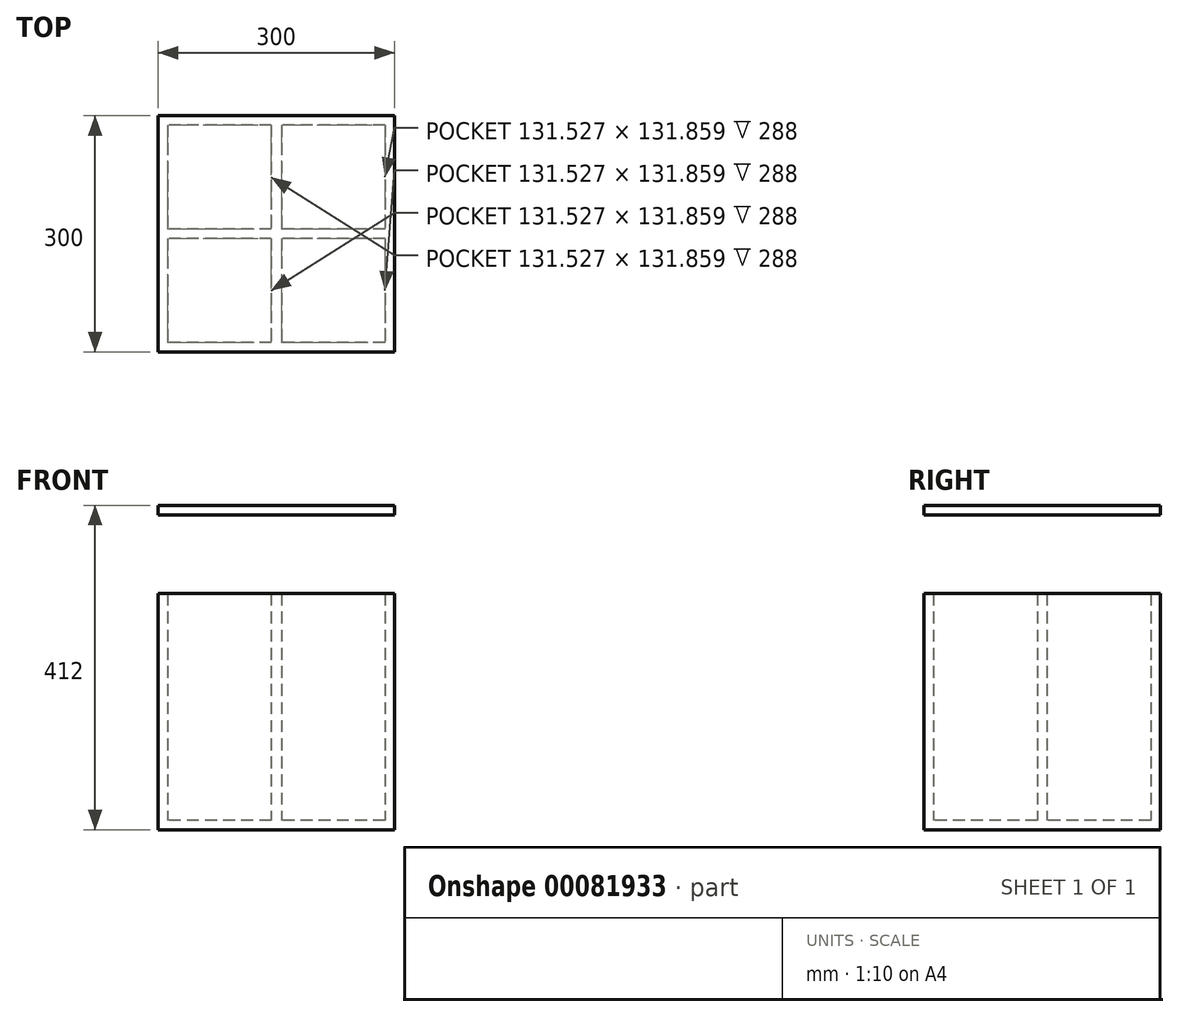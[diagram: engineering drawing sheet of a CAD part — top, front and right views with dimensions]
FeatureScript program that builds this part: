
annotation { "Feature Type Name" : "Feature", "Feature Type Description" : "" }
export const myFeature = defineFeature(function(context is Context, id is Id, definition is map)
    precondition{}
    {
        {
            var Q0;
            Q0=qCreatedBy(makeId("Top.planeOp"),FACE);
            var sketch = newSketch(context, id + "F0", { "sketchPlane" : qUnion([Q0])});
            skLineSegment(sketch, "E0.bottom", {"start": v(150, 150) * mm, "end": v(-150, 150) * mm});
            skLineSegment(sketch, "E0.top", {"start": v(150, -150) * mm, "end": v(-150, -150) * mm});
            skLineSegment(sketch, "E0.left", {"start": v(150, 150) * mm, "end": v(150, -150) * mm});
            skLineSegment(sketch, "E0.right", {"start": v(-150, 150) * mm, "end": v(-150, -150) * mm});
            skPoint(sketch, "E0.middle", {"position": v(0, 0) * mm});
            skSolve(sketch);
        }
        {
            var Q0;
            Q0=makeQuery(id+"F0.imprint","IMPRINT",FACE,{"disambiguationData":[TD([[makeQuery(id+"F0.imprint","IMPRINT",EDGE,{"derivedFrom":sQuery(id+"F0.wireOp",EDGE,"E0.bottom")}),1.0]])]});
            extrude(context, id + "F1", {"entities" : qUnion([Q0]), "depth" : 300 * mm});
        }
        {
            var Q0;
            Q0=makeQuery(id+"F1.opExtrude","CAP_FACE",FACE,{"disambiguationData":[OSD([sQuery(id+"F0.wireOp",EDGE,"E0.bottom"),sQuery(id+"F0.wireOp",EDGE,"E0.top"),sQuery(id+"F0.wireOp",EDGE,"E0.left"),sQuery(id+"F0.wireOp",EDGE,"E0.right")])],"isStart":false});
            shell(context, id + "F2", {"entities" : qUnion([Q0]), "thickness" : 12 * mm});
        }
        {
            var Q0;
            Q0=makeQuery(id+"F2.opShell","OFFSET_FACE",FACE,{"disambiguationData":[OSD([sQuery(id+"F0.wireOp",EDGE,"E0.bottom"),sQuery(id+"F0.wireOp",EDGE,"E0.top"),sQuery(id+"F0.wireOp",EDGE,"E0.left"),sQuery(id+"F0.wireOp",EDGE,"E0.right")])]});
            var sketch = newSketch(context, id + "F3", { "sketchPlane" : qUnion([Q0])});
            skLineSegment(sketch, "E1.bottom", {"start": v(6.47, 138) * mm, "end": v(-6.47, 138) * mm});
            skLineSegment(sketch, "E1.top", {"start": v(6.47, -138) * mm, "end": v(-6.47, -138) * mm});
            skLineSegment(sketch, "E1.left", {"start": v(6.47, 138) * mm, "end": v(6.47, -138) * mm});
            skLineSegment(sketch, "E1.right", {"start": v(-6.47, 138) * mm, "end": v(-6.47, -138) * mm});
            skPoint(sketch, "E1.middle", {"position": v(0, 0) * mm});
            skLineSegment(sketch, "E2.bottom", {"start": v(138, 6.14) * mm, "end": v(-138, 6.14) * mm});
            skLineSegment(sketch, "E2.top", {"start": v(138, -6.14) * mm, "end": v(-138, -6.14) * mm});
            skLineSegment(sketch, "E2.left", {"start": v(138, 6.14) * mm, "end": v(138, -6.14) * mm});
            skLineSegment(sketch, "E2.right", {"start": v(-138, 6.14) * mm, "end": v(-138, -6.14) * mm});
            skSolve(sketch);
        }
        {
            var Q0;
            {var subQ5=sQuery(id+"F3.wireOp",EDGE,"E2.right");Q0=makeQuery(id+"F3.imprint","IMPRINT",FACE,{"disambiguationData":[TD([[makeQuery(id+"F3.imprint","IMPRINT",EDGE,{"derivedFrom":subQ5}),1.0]])]});}
            var Q1;
            {var subQ0=sQuery(id+"F3.wireOp",EDGE,"E2.bottom");var subQ1=sQuery(id+"F3.wireOp",EDGE,"E1.left");var subQ2=makeQuery(id+"F3.imprint","INTERSECT",VERTEX,{"derivedFrom":[subQ1,subQ0]});Q1=makeQuery(id+"F3.imprint","IMPRINT",FACE,{"disambiguationData":[TD([[makeQuery(id+"F3.imprint","IMPRINT",EDGE,{"disambiguationData":[TD([[subQ2,-1.0]])],"derivedFrom":subQ1}),-1.0]])]});}
            var Q2;
            {var subQ0=sQuery(id+"F3.wireOp",EDGE,"E1.bottom");Q2=makeQuery(id+"F3.imprint","IMPRINT",FACE,{"disambiguationData":[TD([[makeQuery(id+"F3.imprint","IMPRINT",EDGE,{"derivedFrom":subQ0}),1.0]])]});}
            var Q3;
            {var subQ5=sQuery(id+"F3.wireOp",EDGE,"E2.left");Q3=makeQuery(id+"F3.imprint","IMPRINT",FACE,{"disambiguationData":[TD([[makeQuery(id+"F3.imprint","IMPRINT",EDGE,{"derivedFrom":subQ5}),-1.0]])]});}
            var Q4;
            {var subQ0=sQuery(id+"F3.wireOp",EDGE,"E1.top");Q4=makeQuery(id+"F3.imprint","IMPRINT",FACE,{"disambiguationData":[TD([[makeQuery(id+"F3.imprint","IMPRINT",EDGE,{"derivedFrom":subQ0}),-1.0]])]});}
            extrude(context, id + "F4", {"entities" : qUnion([Q0, Q1, Q2, Q3, Q4]), "operationType" : NewBodyOperationType.ADD, "depth" : 288 * mm});
        }
        {
            var Q0;
            Q0=makeQuery(id+"F4.boolean.opBoolean","MERGE",FACE,{"derivedFrom":[makeQuery(id+"F1.opExtrude","CAP_FACE",FACE,{"disambiguationData":[OSD([sQuery(id+"F0.wireOp",EDGE,"E0.bottom"),sQuery(id+"F0.wireOp",EDGE,"E0.top"),sQuery(id+"F0.wireOp",EDGE,"E0.left"),sQuery(id+"F0.wireOp",EDGE,"E0.right")])],"isStart":false}),makeQuery(id+"F4.opExtrude","CAP_FACE",FACE,{"disambiguationData":[OSD([sQuery(id+"F3.wireOp",EDGE,"E1.bottom"),sQuery(id+"F3.wireOp",EDGE,"E1.top"),sQuery(id+"F3.wireOp",EDGE,"E1.left"),sQuery(id+"F3.wireOp",EDGE,"E1.right"),sQuery(id+"F3.wireOp",EDGE,"E2.bottom"),sQuery(id+"F3.wireOp",EDGE,"E2.top"),sQuery(id+"F3.wireOp",EDGE,"E2.left"),sQuery(id+"F3.wireOp",EDGE,"E2.right")])],"isStart":false})]});
            cPlane(context, id + "F5", {"entities" : qUnion([Q0]), "cplaneType" : CPlaneType.OFFSET, "offset" : 100 * mm, "width" : 150 * mm, "height" : 150 * mm});
        }
        {
            var Q0;
            Q0=qCreatedBy(id+"F5.planeOp",FACE);
            var sketch = newSketch(context, id + "F6", { "sketchPlane" : qUnion([Q0])});
            skLineSegment(sketch, "E3.bottom", {"start": v(-150, 150) * mm, "end": v(150, 150) * mm});
            skLineSegment(sketch, "E3.top", {"start": v(-150, -150) * mm, "end": v(150, -150) * mm});
            skLineSegment(sketch, "E3.left", {"start": v(-150, 150) * mm, "end": v(-150, -150) * mm});
            skLineSegment(sketch, "E3.right", {"start": v(150, 150) * mm, "end": v(150, -150) * mm});
            skPoint(sketch, "E3.middle", {"position": v(0, 0) * mm});
            skSolve(sketch);
        }
        {
            var Q0;
            Q0=makeQuery(id+"F6.imprint","IMPRINT",FACE,{"disambiguationData":[TD([[makeQuery(id+"F6.imprint","IMPRINT",EDGE,{"derivedFrom":sQuery(id+"F6.wireOp",EDGE,"E3.bottom")}),-1.0]])]});
            extrude(context, id + "F7", {"entities" : qUnion([Q0]), "depth" : 12 * mm});
        }
    });
